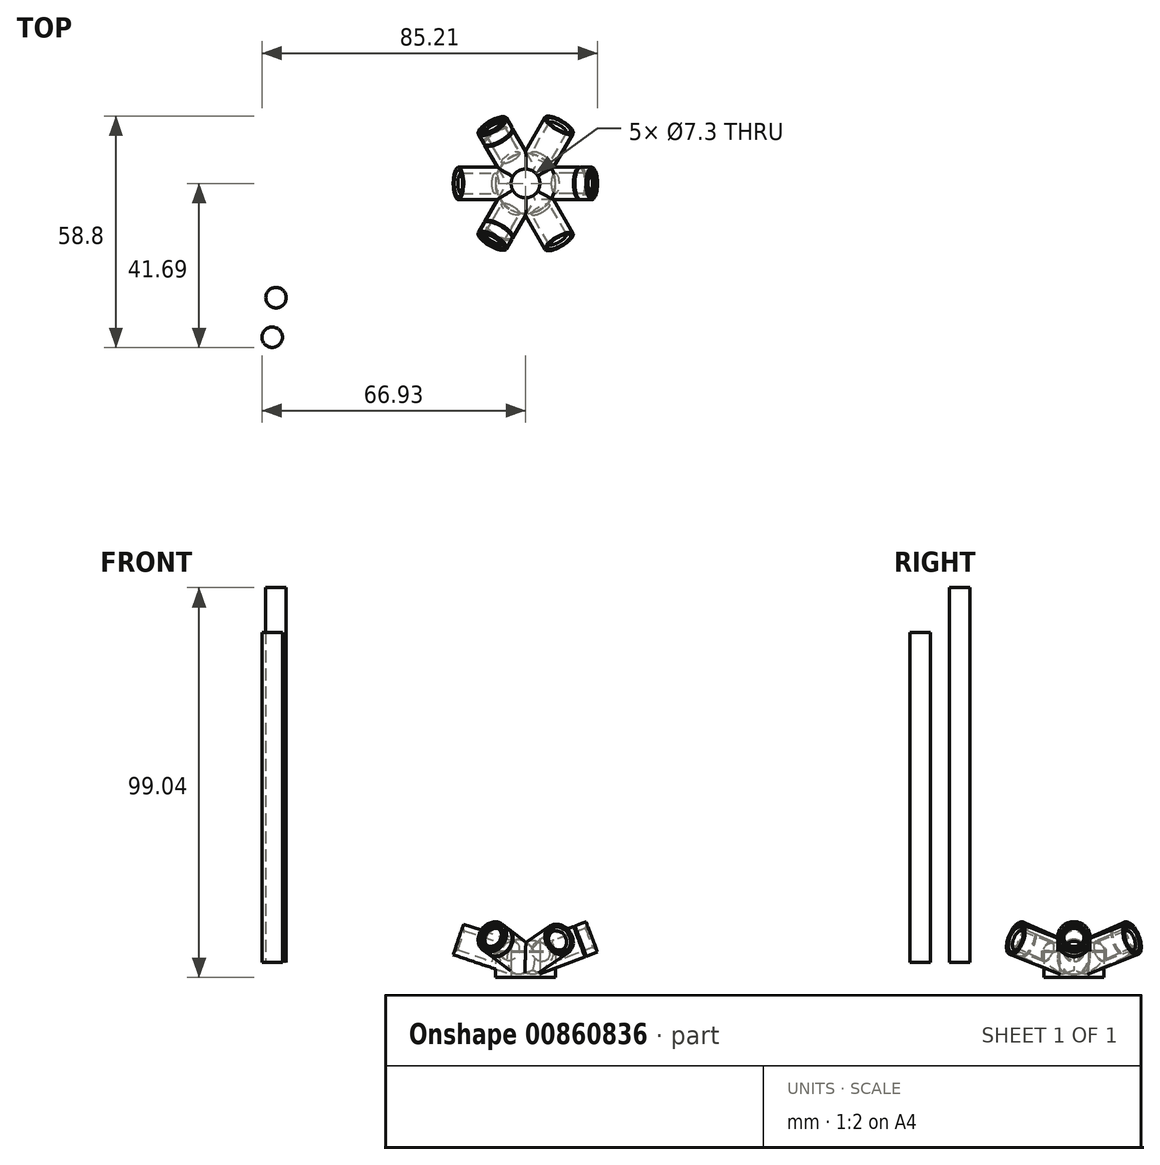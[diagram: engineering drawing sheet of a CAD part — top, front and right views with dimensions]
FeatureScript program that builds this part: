
annotation { "Feature Type Name" : "Feature", "Feature Type Description" : "" }
export const myFeature = defineFeature(function(context is Context, id is Id, definition is map)
    precondition{}
    {
        {
            assignVariable(context, id + "F0", {"name" : "espesor", "anyValue" : 1.5});
        }
        {
            assignVariable(context, id + "F1", {"name" : "longitud", "anyValue" : 18});
        }
        {
            assignVariable(context, id + "F2", {"name" : "relacion", "anyValue" : 1.11});
        }
        {
            assignVariable(context, id + "F3", {"name" : "lvarilla", "anyValue" : 100});
        }
        {
            assignVariable(context, id + "F4", {"name" : "lrecortada", "anyValue" : getVariable(context, 'lvarilla') - 2 * (getVariable(context, 'longitud') * 1.8 / 4)});
        }
        {
            assignVariable(context, id + "F5", {"name" : "lrecortadalarga", "anyValue" : (getVariable(context, 'lvarilla') * getVariable(context, 'relacion') - 2 * (getVariable(context, 'longitud') * 1.8 / 4))});
        }
        {
            var Q0;
            Q0=qCreatedBy(makeId("Front.planeOp"),FACE);
            var sketch = newSketch(context, id + "F6", { "sketchPlane" : qUnion([Q0])});
            skLineSegment(sketch, "E0", {"start": v(0, 0) * mm, "end": v(16.82, 6.42) * mm, "construction": true});
            skLineSegment(sketch, "E1", {"start": v(0, 0) * mm, "end": v(1.46, -3.83) * mm});
            skLineSegment(sketch, "E2", {"start": v(16.82, 6.42) * mm, "end": v(18.28, 2.6) * mm});
            skLineSegment(sketch, "E3", {"start": v(1.46, -3.83) * mm, "end": v(15.1, 1.38) * mm});
            skLineSegment(sketch, "E4", {"start": v(17.74, 4) * mm, "end": v(8.5, 0.46) * mm});
            skLineSegment(sketch, "E5", {"start": v(8.5, 0.46) * mm, "end": v(7.57, 2.9) * mm});
            skLineSegment(sketch, "E6", {"start": v(7.57, 2.9) * mm, "end": v(0, 0) * mm});
            skLineSegment(sketch, "E7", {"start": v(0, 0) * mm, "end": v(0, 41.35) * mm, "construction": true});
            skLineSegment(sketch, "E8", {"start": v(1.46, -3.83) * mm, "end": v(0, -3.83) * mm, "construction": true});
            skLineSegment(sketch, "E9", {"start": v(7.57, 2.9) * mm, "end": v(7.57, -3.83) * mm, "construction": true});
            skLineSegment(sketch, "E10", {"start": v(7.57, -3.83) * mm, "end": v(1.46, -3.83) * mm, "construction": true});
            skLineSegment(sketch, "E11", {"start": v(0, -3.83) * mm, "end": v(7.57, -3.83) * mm});
            skLineSegment(sketch, "E12", {"start": v(7.57, -3.83) * mm, "end": v(7.57, 2.9) * mm});
            skLineSegment(sketch, "E13", {"start": v(0, 2.9) * mm, "end": v(7.57, 2.9) * mm});
            skLineSegment(sketch, "E14", {"start": v(0, 2.9) * mm, "end": v(0, -3.83) * mm});
            skLineSegment(sketch, "E15", {"start": v(15.48, 1.52) * mm, "end": v(15.44, 1.62) * mm});
            skLineSegment(sketch, "E16", {"start": v(15.44, 1.62) * mm, "end": v(15.07, 1.47) * mm});
            skLineSegment(sketch, "E17", {"start": v(15.07, 1.47) * mm, "end": v(15.1, 1.38) * mm});
            skLineSegment(sketch, "E18.trimOffspring", {"start": v(15.48, 1.52) * mm, "end": v(18.28, 2.6) * mm});
            skSolve(sketch);
        }
        {
            var Q0;
            Q0=qCreatedBy(makeId("Front.planeOp"),FACE);
            var sketch = newSketch(context, id + "F7", { "sketchPlane" : qUnion([Q0])});
            skLineSegment(sketch, "E19", {"start": v(0, 0) * mm, "end": v(0, 45.08) * mm, "construction": true});
            skLineSegment(sketch, "E20.MirrorCS", {"start": v(-8.5, 0.13) * mm, "end": v(-7.67, 2.6) * mm});
            skLineSegment(sketch, "E21.MirrorCS", {"start": v(-17.05, 5.77) * mm, "end": v(-18.36, 1.88) * mm});
            skLineSegment(sketch, "E22.MirrorCS", {"start": v(-7.67, 2.6) * mm, "end": v(0, 0) * mm});
            skLineSegment(sketch, "E23.MirrorCS", {"start": v(0, 0) * mm, "end": v(-17.05, 5.77) * mm, "construction": true});
            skLineSegment(sketch, "E24.MirrorCS", {"start": v(0, 2.6) * mm, "end": v(-7.67, 2.6) * mm});
            skLineSegment(sketch, "E25.MirrorCS", {"start": v(-17.88, 3.3) * mm, "end": v(-8.5, 0.13) * mm});
            skLineSegment(sketch, "E26", {"start": v(-18.36, 1.88) * mm, "end": v(-1.31, -3.88) * mm});
            skLineSegment(sketch, "E27", {"start": v(0, 0) * mm, "end": v(-1.31, -3.88) * mm});
            skLineSegment(sketch, "E28", {"start": v(-1.31, -3.88) * mm, "end": v(-7.67, -3.88) * mm});
            skLineSegment(sketch, "E29", {"start": v(-1.31, -3.88) * mm, "end": v(0, -3.88) * mm});
            skLineSegment(sketch, "E30", {"start": v(0, -3.88) * mm, "end": v(0, 2.6) * mm});
            skLineSegment(sketch, "E31", {"start": v(-7.67, 2.6) * mm, "end": v(-7.67, -3.88) * mm});
            skSolve(sketch);
        }
        {
            var Q0;
            {var subQ1=sQuery(id+"F6.wireOp",EDGE,"E4");Q0=makeQuery(id+"F6.imprint","IMPRINT",FACE,{"disambiguationData":[TD([[makeQuery(id+"F6.imprint","IMPRINT",EDGE,{"derivedFrom":subQ1}),1.0]])]});}
            var Q1;
            {var subQ0=sQuery(id+"F6.wireOp",EDGE,"E1");Q1=makeQuery(id+"F6.imprint","IMPRINT",FACE,{"disambiguationData":[TD([[makeQuery(id+"F6.imprint","IMPRINT",EDGE,{"derivedFrom":subQ0}),1.0]])]});}
            var Q2;
            Q2=sQuery(id+"F6.wireOp",EDGE,"E0");
            revolve(context, id + "F8", {"surfaceOperationType" : NewSurfaceOperationType.NEW, "entities" : qUnion([Q0, Q1]), "axis" : qUnion([Q2]), "revolveType" : RevolveType.FULL});
        }
        {
            var Q0;
            {var subQ5=sQuery(id+"F7.wireOp",EDGE,"E20.MirrorCS");Q0=makeQuery(id+"F7.imprint","IMPRINT",FACE,{"disambiguationData":[TD([[makeQuery(id+"F7.imprint","IMPRINT",EDGE,{"derivedFrom":subQ5}),-1.0]])]});}
            var Q1;
            {var subQ0=sQuery(id+"F7.wireOp",EDGE,"E22.MirrorCS");Q1=makeQuery(id+"F7.imprint","IMPRINT",FACE,{"disambiguationData":[TD([[makeQuery(id+"F7.imprint","IMPRINT",EDGE,{"derivedFrom":subQ0}),-1.0]])]});}
            var Q2;
            Q2=sQuery(id+"F7.wireOp",EDGE,"E23.MirrorCS");
            revolve(context, id + "F9", {"surfaceOperationType" : NewSurfaceOperationType.NEW, "entities" : qUnion([Q0, Q1]), "axis" : qUnion([Q2]), "revolveType" : RevolveType.FULL});
        }
        {
            var Q0;
            Q0=makeQuery(id+"F8.opRevolve","SWEPT_BODY",BODY,{"disambiguationData":[OSD([sQuery(id+"F6.wireOp",EDGE,"E1"),sQuery(id+"F6.wireOp",EDGE,"E2"),sQuery(id+"F6.wireOp",EDGE,"E3"),sQuery(id+"F6.wireOp",EDGE,"E4"),sQuery(id+"F6.wireOp",EDGE,"E5"),sQuery(id+"F6.wireOp",EDGE,"E6")])]});
            var Q1;
            Q1=sQuery(id+"F6.wireOp",EDGE,"E7");
            circularPattern(context, id + "F10", {"operationType" : NewBodyOperationType.ADD, "entities" : qUnion([Q0]), "axis" : qUnion([Q1]), "angle" : 360 * degree, "instanceCount" : 3, "equalSpace" : true});
        }
        {
            var Q0;
            Q0=makeQuery(id+"FgpRCOrkwi8NXZ9_2.boolean.opBoolean","SPLIT",BODY,{"disambiguationData":[OD(1.0)],"derivedFrom":makeQuery(id+"F9.opRevolve","SWEPT_BODY",BODY,{"disambiguationData":[OSD([sQuery(id+"F7.wireOp",EDGE,"E20.MirrorCS"),sQuery(id+"F7.wireOp",EDGE,"E21.MirrorCS"),sQuery(id+"F7.wireOp",EDGE,"E22.MirrorCS"),sQuery(id+"F7.wireOp",EDGE,"E25.MirrorCS"),sQuery(id+"F7.wireOp",EDGE,"E26"),sQuery(id+"F7.wireOp",EDGE,"E27")])]})});
            var Q1;
            Q1=sQuery(id+"F7.wireOp",EDGE,"E19");
            circularPattern(context, id + "F11", {"entities" : qUnion([Q0]), "axis" : qUnion([Q1]), "angle" : 360 * degree, "instanceCount" : 3, "equalSpace" : true});
        }
        {
            var Q0;
            {var subQ0=sQuery(id+"F6.wireOp",EDGE,"E1");Q0=makeQuery(id+"F6.imprint","IMPRINT",FACE,{"disambiguationData":[TD([[makeQuery(id+"F6.imprint","IMPRINT",EDGE,{"derivedFrom":subQ0}),-1.0]])]});}
            var Q1;
            {var subQ0=sQuery(id+"F6.wireOp",EDGE,"E1");Q1=makeQuery(id+"F6.imprint","IMPRINT",FACE,{"disambiguationData":[TD([[makeQuery(id+"F6.imprint","IMPRINT",EDGE,{"derivedFrom":subQ0}),1.0]])]});}
            var Q2;
            {var subQ0=sQuery(id+"F6.wireOp",EDGE,"E11");var subQ3=sQuery(id+"F6.wireOp",EDGE,"E12");var subQ5=makeQuery(id+"F6.imprint","INTERSECT",VERTEX,{"derivedFrom":[subQ0,subQ3]});Q2=makeQuery(id+"F6.imprint","IMPRINT",FACE,{"disambiguationData":[TD([[makeQuery(id+"F6.imprint","IMPRINT",EDGE,{"disambiguationData":[TD([[subQ5,-1.0]])],"derivedFrom":subQ3}),1.0]])]});}
            var Q3;
            {var subQ0=sQuery(id+"F6.wireOp",EDGE,"E6");Q3=makeQuery(id+"F6.imprint","IMPRINT",FACE,{"disambiguationData":[TD([[makeQuery(id+"F6.imprint","IMPRINT",EDGE,{"derivedFrom":subQ0}),-1.0]])]});}
            var Q4;
            Q4=sQuery(id+"F6.wireOp",EDGE,"E13");
            var Q5;
            Q5=sQuery(id+"F6.wireOp",EDGE,"E14");
            var Q6;
            Q6=sQuery(id+"F6.wireOp",EDGE,"E7");
            revolve(context, id + "F12", {"surfaceOperationType" : NewSurfaceOperationType.NEW, "entities" : qUnion([Q0, Q1, Q2, Q3]), "surfaceEntities" : qUnion([Q4, Q5]), "axis" : qUnion([Q6]), "revolveType" : RevolveType.FULL});
        }
        {
            var Q0;
            {var subQ0=sQuery(id+"F7.wireOp",EDGE,"E22.MirrorCS");Q0=makeQuery(id+"F7.imprint","IMPRINT",FACE,{"disambiguationData":[TD([[makeQuery(id+"F7.imprint","IMPRINT",EDGE,{"derivedFrom":subQ0}),1.0]])]});}
            var Q1;
            {var subQ0=sQuery(id+"F7.wireOp",EDGE,"E22.MirrorCS");Q1=makeQuery(id+"F7.imprint","IMPRINT",FACE,{"disambiguationData":[TD([[makeQuery(id+"F7.imprint","IMPRINT",EDGE,{"derivedFrom":subQ0}),-1.0]])]});}
            var Q2;
            {var subQ0=sQuery(id+"F7.wireOp",EDGE,"E27");Q2=makeQuery(id+"F7.imprint","IMPRINT",FACE,{"disambiguationData":[TD([[makeQuery(id+"F7.imprint","IMPRINT",EDGE,{"derivedFrom":subQ0}),1.0]])]});}
            var Q3;
            {var subQ0=sQuery(id+"F7.wireOp",EDGE,"E28");Q3=makeQuery(id+"F7.imprint","IMPRINT",FACE,{"disambiguationData":[TD([[makeQuery(id+"F7.imprint","IMPRINT",EDGE,{"derivedFrom":subQ0}),-1.0]])]});}
            var Q4;
            Q4=sQuery(id+"F7.wireOp",EDGE,"E19");
            revolve(context, id + "F13", {"surfaceOperationType" : NewSurfaceOperationType.NEW, "entities" : qUnion([Q0, Q1, Q2, Q3]), "axis" : qUnion([Q4]), "revolveType" : RevolveType.FULL});
        }
        {
            var Q0;
            Q0=makeQuery(id+"F10.opPattern","COPY",EDGE,{"derivedFrom":makeQuery(id+"F8.opRevolve","SWEPT_EDGE",EDGE,{"disambiguationData":[OSD([sQuery(id+"F6.wireOp",EDGE,"E2"),sQuery(id+"F6.wireOp",EDGE,"E4")])]}),"instanceName":"5"});
            var Q1;
            Q1=makeQuery(id+"F10.opPattern","COPY",EDGE,{"derivedFrom":makeQuery(id+"F8.opRevolve","SWEPT_EDGE",EDGE,{"disambiguationData":[OSD([sQuery(id+"F6.wireOp",EDGE,"E2"),sQuery(id+"F6.wireOp",EDGE,"E4")])]}),"instanceName":"4"});
            var Q2;
            Q2=makeQuery(id+"F8.opRevolve","SWEPT_EDGE",EDGE,{"disambiguationData":[OSD([sQuery(id+"F6.wireOp",EDGE,"E2"),sQuery(id+"F6.wireOp",EDGE,"E4")])]});
            var Q3;
            Q3=makeQuery(id+"F10.opPattern","COPY",EDGE,{"derivedFrom":makeQuery(id+"F8.opRevolve","SWEPT_EDGE",EDGE,{"disambiguationData":[OSD([sQuery(id+"F6.wireOp",EDGE,"E2"),sQuery(id+"F6.wireOp",EDGE,"E4")])]}),"instanceName":"1"});
            var Q4;
            Q4=makeQuery(id+"F10.opPattern","COPY",EDGE,{"derivedFrom":makeQuery(id+"F8.opRevolve","SWEPT_EDGE",EDGE,{"disambiguationData":[OSD([sQuery(id+"F6.wireOp",EDGE,"E2"),sQuery(id+"F6.wireOp",EDGE,"E4")])]}),"instanceName":"2"});
            var Q5;
            Q5=makeQuery(id+"F10.opPattern","COPY",EDGE,{"derivedFrom":makeQuery(id+"F8.opRevolve","SWEPT_EDGE",EDGE,{"disambiguationData":[OSD([sQuery(id+"F6.wireOp",EDGE,"E2"),sQuery(id+"F6.wireOp",EDGE,"E4")])]}),"instanceName":"3"});
            var Q6;
            Q6=makeQuery(id+"F11.opPattern","COPY",EDGE,{"derivedFrom":makeQuery(id+"F9.opRevolve","SWEPT_EDGE",EDGE,{"disambiguationData":[OSD([sQuery(id+"F7.wireOp",EDGE,"E21.MirrorCS"),sQuery(id+"F7.wireOp",EDGE,"E25.MirrorCS")])]}),"instanceName":"2"});
            var Q7;
            Q7=makeQuery(id+"F9.opRevolve","SWEPT_EDGE",EDGE,{"disambiguationData":[OSD([sQuery(id+"F7.wireOp",EDGE,"E21.MirrorCS"),sQuery(id+"F7.wireOp",EDGE,"E25.MirrorCS")])]});
            var Q8;
            Q8=makeQuery(id+"F11.opPattern","COPY",EDGE,{"derivedFrom":makeQuery(id+"F9.opRevolve","SWEPT_EDGE",EDGE,{"disambiguationData":[OSD([sQuery(id+"F7.wireOp",EDGE,"E21.MirrorCS"),sQuery(id+"F7.wireOp",EDGE,"E25.MirrorCS")])]}),"instanceName":"1"});
            chamfer(context, id + "F14", {"entities" : qUnion([Q0, Q1, Q2, Q3, Q4, Q5, Q6, Q7, Q8]), "width" : (getVariable(context, 'espesor') / 2) * mm, "tangentPropagation" : true});
        }
        {
            var Q0;
            Q0=qCreatedBy(makeId("Top.planeOp"),FACE);
            var sketch = newSketch(context, id + "F15", { "sketchPlane" : qUnion([Q0])});
            skCircle(sketch, "E32", {"center": v(-64.33, -39.09) * mm, "radius": 2.6 * mm});
            skCircle(sketch, "E33", {"center": v(-63.38, -29.03) * mm, "radius": 2.6 * mm});
            skSolve(sketch);
        }
        {
            var Q0;
            Q0=makeQuery(id+"F15.imprint","IMPRINT",FACE,{"disambiguationData":[TD([[makeQuery(id+"F15.imprint","IMPRINT",EDGE,{"derivedFrom":sQuery(id+"F15.wireOp",EDGE,"E32")}),1.0]])]});
            extrude(context, id + "F16", {"entities" : qUnion([Q0]), "depth" : (getVariable(context, 'lrecortada')) * mm, "offsetDistance" : 25 * mm});
        }
        {
            var Q0;
            Q0=makeQuery(id+"F15.imprint","IMPRINT",FACE,{"disambiguationData":[TD([[makeQuery(id+"F15.imprint","IMPRINT",EDGE,{"derivedFrom":sQuery(id+"F15.wireOp",EDGE,"E33")}),1.0]])]});
            extrude(context, id + "F17", {"entities" : qUnion([Q0]), "depth" : (getVariable(context, 'lrecortadalarga')) * mm, "offsetDistance" : 25 * mm});
        }
        {
            var Q0;
            Q0=qCreatedBy(makeId("Top.planeOp"),FACE);
            var sketch = newSketch(context, id + "F18", { "sketchPlane" : qUnion([Q0])});
            skCircle(sketch, "E34", {"center": v(0, 0) * mm, "radius": 3.65 * mm});
            skSolve(sketch);
        }
        {
            var Q0;
            Q0 = qSketchRegion(id + "F18", true);
            extrude(context, id + "F19", {"entities" : qUnion([Q0]), "operationType" : NewBodyOperationType.REMOVE, "depth" : 200 * mm, "offsetDistance" : 25 * mm, "symmetric" : true});
        }
    });
